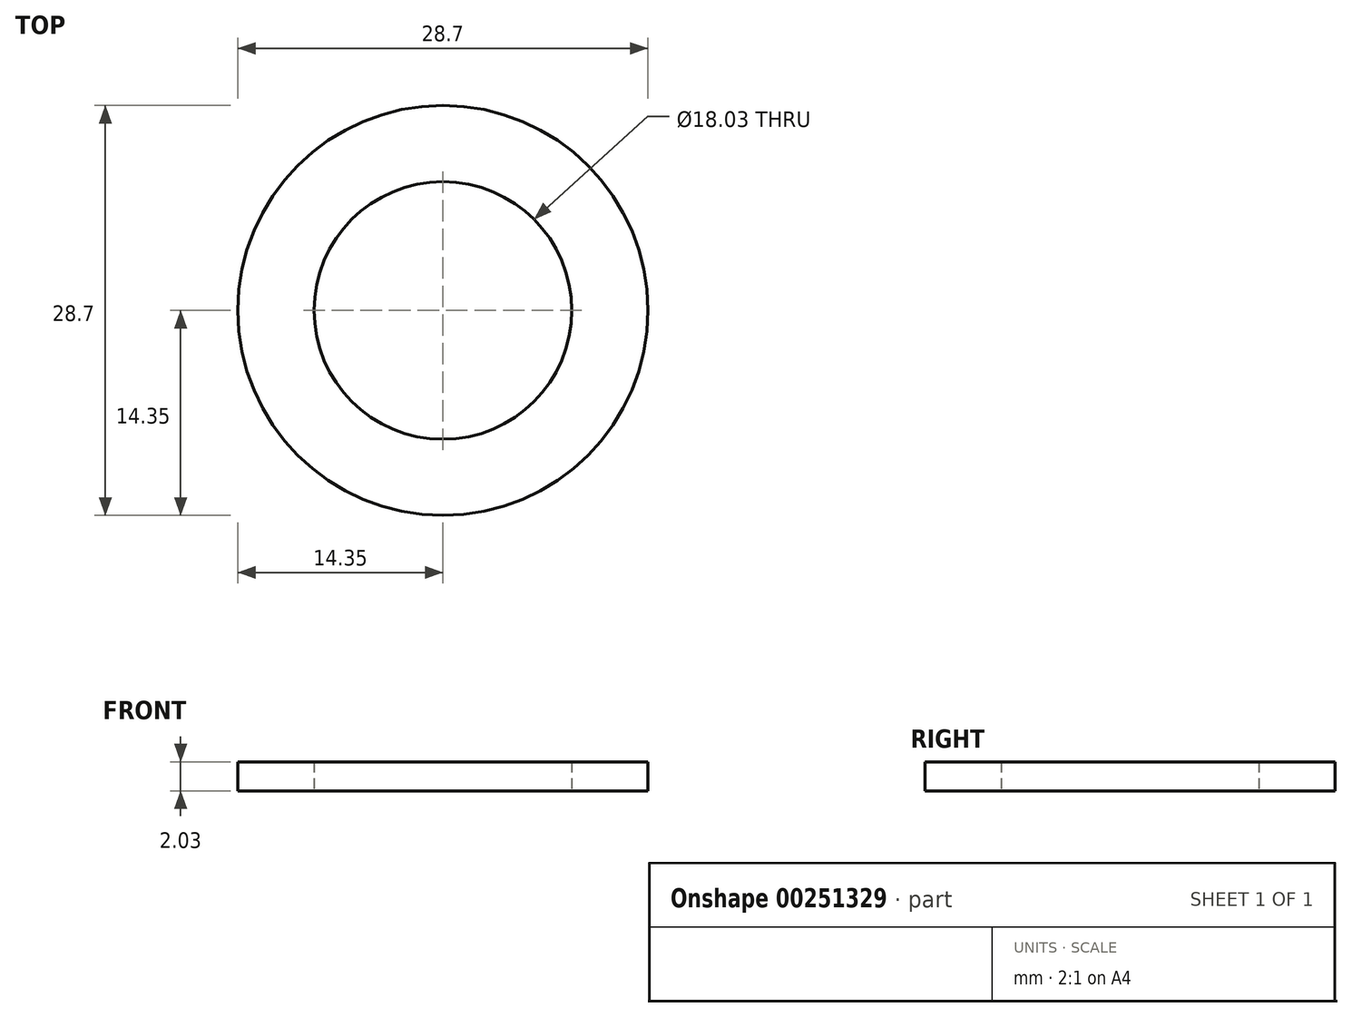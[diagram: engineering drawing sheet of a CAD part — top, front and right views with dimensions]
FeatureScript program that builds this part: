
annotation { "Feature Type Name" : "Feature", "Feature Type Description" : "" }
export const myFeature = defineFeature(function(context is Context, id is Id, definition is map)
    precondition{}
    {
        {
            var Q0;
            Q0=qCreatedBy(makeId("Top.planeOp"),FACE);
            var sketch = newSketch(context, id + "F0", { "sketchPlane" : qUnion([Q0])});
            skCircle(sketch, "E0", {"center": v(0, 0) * mm, "radius": 14.35 * mm});
            skCircle(sketch, "E1", {"center": v(0, 0) * mm, "radius": 9.02 * mm});
            skSolve(sketch);
        }
        {
            var Q0;
            Q0=makeQuery(id+"F0.imprint","IMPRINT",FACE,{"disambiguationData":[TD([[makeQuery(id+"F0.imprint","IMPRINT",EDGE,{"derivedFrom":sQuery(id+"F0.wireOp",EDGE,"E0")}),1.0]])]});
            extrude(context, id + "F1", {"entities" : qUnion([Q0]), "depth" : 2.03 * mm});
        }
    });
